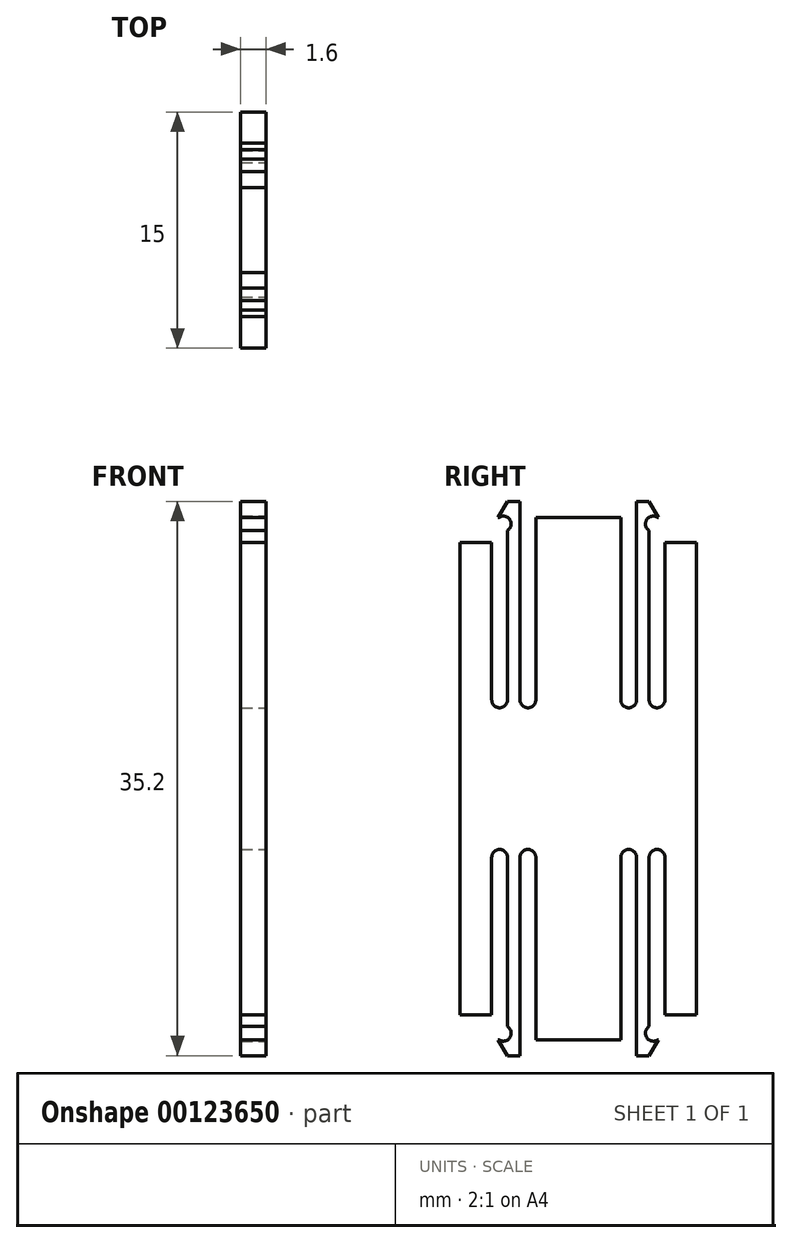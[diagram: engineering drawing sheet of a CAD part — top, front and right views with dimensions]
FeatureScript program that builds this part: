
annotation { "Feature Type Name" : "Feature", "Feature Type Description" : "" }
export const myFeature = defineFeature(function(context is Context, id is Id, definition is map)
    precondition{}
    {
        {
            var Q0;
            Q0=qCreatedBy(makeId("Right.planeOp"),FACE);
            var sketch = newSketch(context, id + "F3", { "sketchPlane" : qUnion([Q0])});
            skLineSegment(sketch, "E0.bottom", {"start": v(0, 0) * mm, "end": v(15, 0) * mm});
            skLineSegment(sketch, "E0.top", {"start": v(0, 30) * mm, "end": v(15, 30) * mm});
            skLineSegment(sketch, "E0.left", {"start": v(0, 0) * mm, "end": v(0, 30) * mm});
            skLineSegment(sketch, "E0.right", {"start": v(15, 0) * mm, "end": v(15, 30) * mm});
            skSolve(sketch);
        }
        {
            var Q0;
            Q0=makeQuery(id+"F3.imprint","IMPRINT",FACE,{"disambiguationData":[TD([[makeQuery(id+"F3.imprint","IMPRINT",EDGE,{"derivedFrom":sQuery(id+"F3.wireOp",EDGE,"E0.bottom")}),1.0]])]});
            extrude(context, id + "F4", {"entities" : qUnion([Q0]), "depth" : 1.6 * mm});
        }
        {
            var Q0;
            Q0=makeQuery(id+"F4.opExtrude","CAP_FACE",FACE,{"disambiguationData":[OSD([sQuery(id+"F3.wireOp",EDGE,"E0.bottom"),sQuery(id+"F3.wireOp",EDGE,"E0.top"),sQuery(id+"F3.wireOp",EDGE,"E0.left"),sQuery(id+"F3.wireOp",EDGE,"E0.right")])],"isStart":false});
            var sketch = newSketch(context, id + "F5", { "sketchPlane" : qUnion([Q0])});
            skLineSegment(sketch, "E1", {"start": v(2, 30) * mm, "end": v(2, 20) * mm});
            skLineSegment(sketch, "E2", {"start": v(2, 20) * mm, "end": v(3, 20) * mm});
            skLineSegment(sketch, "E3", {"start": v(3, 20) * mm, "end": v(3, 30) * mm});
            skLineSegment(sketch, "E4", {"start": v(3.8, 30) * mm, "end": v(3.8, 20) * mm});
            skLineSegment(sketch, "E5", {"start": v(3.8, 20) * mm, "end": v(4.8, 20) * mm});
            skLineSegment(sketch, "E6", {"start": v(4.8, 20) * mm, "end": v(4.8, 30) * mm});
            skLineSegment(sketch, "E7", {"start": v(2, 30) * mm, "end": v(3, 30) * mm});
            skLineSegment(sketch, "E8", {"start": v(3.8, 30) * mm, "end": v(4.8, 30) * mm});
            skLineSegment(sketch, "E9", {"start": v(7.5, 30) * mm, "end": v(7.5, 0) * mm, "construction": true});
            skLineSegment(sketch, "E10", {"start": v(0, 15) * mm, "end": v(15, 15) * mm, "construction": true});
            skLineSegment(sketch, "E11.MirrorCS", {"start": v(10.2, 20) * mm, "end": v(10.2, 30) * mm});
            skLineSegment(sketch, "E12.MirrorCS", {"start": v(12, 20) * mm, "end": v(12, 30) * mm});
            skLineSegment(sketch, "E13.MirrorCS", {"start": v(13, 30) * mm, "end": v(13, 20) * mm});
            skLineSegment(sketch, "E14.MirrorCS", {"start": v(11.2, 30) * mm, "end": v(11.2, 20) * mm});
            skLineSegment(sketch, "E15.MirrorCS", {"start": v(11.2, 20) * mm, "end": v(10.2, 20) * mm});
            skLineSegment(sketch, "E16.MirrorCS", {"start": v(13, 20) * mm, "end": v(12, 20) * mm});
            skLineSegment(sketch, "E17.MirrorCS", {"start": v(11.2, 30) * mm, "end": v(10.2, 30) * mm});
            skLineSegment(sketch, "E18.MirrorCS", {"start": v(13, 30) * mm, "end": v(12, 30) * mm});
            skLineSegment(sketch, "E19.MirrorCS", {"start": v(12, 10) * mm, "end": v(12, 0) * mm});
            skLineSegment(sketch, "E20.MirrorCS", {"start": v(13, 0) * mm, "end": v(13, 10) * mm});
            skLineSegment(sketch, "E21.MirrorCS", {"start": v(13, 10) * mm, "end": v(12, 10) * mm});
            skLineSegment(sketch, "E22.MirrorCS", {"start": v(11.2, 10) * mm, "end": v(10.2, 10) * mm});
            skLineSegment(sketch, "E23.MirrorCS", {"start": v(11.2, 0) * mm, "end": v(10.2, 0) * mm});
            skLineSegment(sketch, "E24.MirrorCS", {"start": v(13, 0) * mm, "end": v(12, 0) * mm});
            skLineSegment(sketch, "E25.MirrorCS", {"start": v(10.2, 10) * mm, "end": v(10.2, 0) * mm});
            skLineSegment(sketch, "E26.MirrorCS", {"start": v(11.2, 0) * mm, "end": v(11.2, 10) * mm});
            skLineSegment(sketch, "E27.MirrorCS", {"start": v(4.8, 10) * mm, "end": v(4.8, 0) * mm});
            skLineSegment(sketch, "E28.MirrorCS", {"start": v(3.8, 0) * mm, "end": v(3.8, 10) * mm});
            skLineSegment(sketch, "E29.MirrorCS", {"start": v(3, 10) * mm, "end": v(3, 0) * mm});
            skLineSegment(sketch, "E30.MirrorCS", {"start": v(2, 10) * mm, "end": v(3, 10) * mm});
            skLineSegment(sketch, "E31.MirrorCS", {"start": v(3.8, 10) * mm, "end": v(4.8, 10) * mm});
            skLineSegment(sketch, "E32.MirrorCS", {"start": v(2, 0) * mm, "end": v(3, 0) * mm});
            skLineSegment(sketch, "E33.MirrorCS", {"start": v(3.8, 0) * mm, "end": v(4.8, 0) * mm});
            skLineSegment(sketch, "E34.MirrorCS", {"start": v(2, 0) * mm, "end": v(2, 10) * mm});
            skSolve(sketch);
        }
        {
            var Q0;
            Q0 = qSketchRegion(id + "F5", true);
            extrude(context, id + "F0", {"entities" : qUnion([Q0]), "operationType" : NewBodyOperationType.REMOVE, "oppositeDirection" : true, "depth" : 25 * mm});
        }
        {
            var Q0;
            Q0=makeQuery(id+"F4.opExtrude","CAP_FACE",FACE,{"disambiguationData":[OSD([sQuery(id+"F3.wireOp",EDGE,"E0.bottom"),sQuery(id+"F3.wireOp",EDGE,"E0.top"),sQuery(id+"F3.wireOp",EDGE,"E0.left"),sQuery(id+"F3.wireOp",EDGE,"E0.right")])],"isStart":false});
            var sketch = newSketch(context, id + "F6", { "sketchPlane" : qUnion([Q0])});
            skLineSegment(sketch, "E35", {"start": v(3.8, 30) * mm, "end": v(3.8, 32.6) * mm});
            skLineSegment(sketch, "E36", {"start": v(3.8, 32.6) * mm, "end": v(3, 32.6) * mm});
            skLineSegment(sketch, "E37", {"start": v(3, 32.6) * mm, "end": v(2.4, 31.6) * mm});
            skLineSegment(sketch, "E38", {"start": v(2.4, 31.6) * mm, "end": v(3, 31.6) * mm});
            skLineSegment(sketch, "E39", {"start": v(3, 31.6) * mm, "end": v(3, 30) * mm});
            skLineSegment(sketch, "E40", {"start": v(3, 30) * mm, "end": v(3, 30) * mm});
            skLineSegment(sketch, "E41.bottom", {"start": v(4.8, 30) * mm, "end": v(7.5, 30) * mm});
            skLineSegment(sketch, "E41.top", {"start": v(4.8, 31.6) * mm, "end": v(7.5, 31.6) * mm});
            skLineSegment(sketch, "E41.left", {"start": v(4.8, 30) * mm, "end": v(4.8, 31.6) * mm});
            skLineSegment(sketch, "E41.right", {"start": v(7.5, 30) * mm, "end": v(7.5, 31.6) * mm});
            skLineSegment(sketch, "E42", {"start": v(0, 15) * mm, "end": v(15, 15) * mm, "construction": true});
            skLineSegment(sketch, "E43", {"start": v(7.5, 15) * mm, "end": v(7.5, 30) * mm, "construction": true});
            skLineSegment(sketch, "E44", {"start": v(3, 30) * mm, "end": v(3.8, 30) * mm});
            skLineSegment(sketch, "E45.MirrorCS", {"start": v(10.2, 30) * mm, "end": v(7.5, 30) * mm});
            skLineSegment(sketch, "E46.MirrorCS", {"start": v(10.2, 31.6) * mm, "end": v(7.5, 31.6) * mm});
            skLineSegment(sketch, "E47.MirrorCS", {"start": v(10.2, 30) * mm, "end": v(10.2, 31.6) * mm});
            skLineSegment(sketch, "E48.MirrorCS", {"start": v(11.2, 32.6) * mm, "end": v(12, 32.6) * mm});
            skLineSegment(sketch, "E49.MirrorCS", {"start": v(12, 32.6) * mm, "end": v(12.6, 31.6) * mm});
            skLineSegment(sketch, "E50.MirrorCS", {"start": v(12.6, 31.6) * mm, "end": v(12, 31.6) * mm});
            skLineSegment(sketch, "E51.MirrorCS", {"start": v(12, 30) * mm, "end": v(11.2, 30) * mm});
            skLineSegment(sketch, "E52.MirrorCS", {"start": v(11.2, 30) * mm, "end": v(11.2, 32.6) * mm});
            skLineSegment(sketch, "E53.MirrorCS", {"start": v(12, 31.6) * mm, "end": v(12, 30) * mm});
            skLineSegment(sketch, "E54.MirrorCS", {"start": v(3, -2.6) * mm, "end": v(2.4, -1.6) * mm});
            skLineSegment(sketch, "E55.MirrorCS", {"start": v(4.8, -1.6) * mm, "end": v(7.5, -1.6) * mm});
            skLineSegment(sketch, "E56.MirrorCS", {"start": v(4.8, 0) * mm, "end": v(4.8, -1.6) * mm});
            skLineSegment(sketch, "E57.MirrorCS", {"start": v(10.2, 0) * mm, "end": v(7.5, 0) * mm});
            skLineSegment(sketch, "E58.MirrorCS", {"start": v(10.2, -1.6) * mm, "end": v(7.5, -1.6) * mm});
            skLineSegment(sketch, "E59.MirrorCS", {"start": v(10.2, 0) * mm, "end": v(10.2, -1.6) * mm});
            skLineSegment(sketch, "E60.MirrorCS", {"start": v(11.2, 0) * mm, "end": v(11.2, -2.6) * mm});
            skLineSegment(sketch, "E61.MirrorCS", {"start": v(12, -1.6) * mm, "end": v(12, 0) * mm});
            skLineSegment(sketch, "E62.MirrorCS", {"start": v(4.8, 0) * mm, "end": v(7.5, 0) * mm});
            skLineSegment(sketch, "E63.MirrorCS", {"start": v(3, -1.6) * mm, "end": v(3, 0) * mm});
            skLineSegment(sketch, "E64.MirrorCS", {"start": v(3.8, 0) * mm, "end": v(3.8, -2.6) * mm});
            skLineSegment(sketch, "E65.MirrorCS", {"start": v(3.8, -2.6) * mm, "end": v(3, -2.6) * mm});
            skLineSegment(sketch, "E66.MirrorCS", {"start": v(2.4, -1.6) * mm, "end": v(3, -1.6) * mm});
            skLineSegment(sketch, "E67.MirrorCS", {"start": v(12, -2.6) * mm, "end": v(12.6, -1.6) * mm});
            skLineSegment(sketch, "E68.MirrorCS", {"start": v(12.6, -1.6) * mm, "end": v(12, -1.6) * mm});
            skLineSegment(sketch, "E69.MirrorCS", {"start": v(11.2, -2.6) * mm, "end": v(12, -2.6) * mm});
            skLineSegment(sketch, "E70.MirrorCS", {"start": v(3, 0) * mm, "end": v(3.8, 0) * mm});
            skLineSegment(sketch, "E71.MirrorCS", {"start": v(12, 0) * mm, "end": v(11.2, 0) * mm});
            skSolve(sketch);
        }
        {
            var Q0;
            Q0 = qSketchRegion(id + "F6", true);
            extrude(context, id + "F1", {"entities" : qUnion([Q0]), "operationType" : NewBodyOperationType.ADD, "oppositeDirection" : true, "depth" : 1.6 * mm});
        }
        {
            var Q0;
            Q0=makeQuery(id+"F1.boolean.opBoolean","MERGE",FACE,{"derivedFrom":[makeQuery(id+"F4.opExtrude","CAP_FACE",FACE,{"disambiguationData":[OSD([sQuery(id+"F3.wireOp",EDGE,"E0.bottom"),sQuery(id+"F3.wireOp",EDGE,"E0.top"),sQuery(id+"F3.wireOp",EDGE,"E0.left"),sQuery(id+"F3.wireOp",EDGE,"E0.right")])],"isStart":false}),makeQuery(id+"F1.opExtrude","CAP_FACE",FACE,{"disambiguationData":[OSD([sQuery(id+"F6.wireOp",EDGE,"E35"),sQuery(id+"F6.wireOp",EDGE,"E36"),sQuery(id+"F6.wireOp",EDGE,"E37"),sQuery(id+"F6.wireOp",EDGE,"E38"),sQuery(id+"F6.wireOp",EDGE,"E39"),sQuery(id+"F6.wireOp",EDGE,"E44")])],"isStart":true}),makeQuery(id+"F1.opExtrude","CAP_FACE",FACE,{"disambiguationData":[OSD([sQuery(id+"F6.wireOp",EDGE,"E41.bottom"),sQuery(id+"F6.wireOp",EDGE,"E41.top"),sQuery(id+"F6.wireOp",EDGE,"E41.left"),sQuery(id+"F6.wireOp",EDGE,"E45.MirrorCS"),sQuery(id+"F6.wireOp",EDGE,"E46.MirrorCS"),sQuery(id+"F6.wireOp",EDGE,"E47.MirrorCS")])],"isStart":true}),makeQuery(id+"F1.opExtrude","CAP_FACE",FACE,{"disambiguationData":[OSD([sQuery(id+"F6.wireOp",EDGE,"E48.MirrorCS"),sQuery(id+"F6.wireOp",EDGE,"E49.MirrorCS"),sQuery(id+"F6.wireOp",EDGE,"E50.MirrorCS"),sQuery(id+"F6.wireOp",EDGE,"E51.MirrorCS"),sQuery(id+"F6.wireOp",EDGE,"E52.MirrorCS"),sQuery(id+"F6.wireOp",EDGE,"E53.MirrorCS")])],"isStart":true}),makeQuery(id+"F1.opExtrude","CAP_FACE",FACE,{"disambiguationData":[OSD([sQuery(id+"F6.wireOp",EDGE,"E54.MirrorCS"),sQuery(id+"F6.wireOp",EDGE,"E63.MirrorCS"),sQuery(id+"F6.wireOp",EDGE,"E64.MirrorCS"),sQuery(id+"F6.wireOp",EDGE,"E65.MirrorCS"),sQuery(id+"F6.wireOp",EDGE,"E66.MirrorCS"),sQuery(id+"F6.wireOp",EDGE,"E70.MirrorCS")])],"isStart":true}),makeQuery(id+"F1.opExtrude","CAP_FACE",FACE,{"disambiguationData":[OSD([sQuery(id+"F6.wireOp",EDGE,"E55.MirrorCS"),sQuery(id+"F6.wireOp",EDGE,"E56.MirrorCS"),sQuery(id+"F6.wireOp",EDGE,"E57.MirrorCS"),sQuery(id+"F6.wireOp",EDGE,"E58.MirrorCS"),sQuery(id+"F6.wireOp",EDGE,"E59.MirrorCS"),sQuery(id+"F6.wireOp",EDGE,"E62.MirrorCS")])],"isStart":true}),makeQuery(id+"F1.opExtrude","CAP_FACE",FACE,{"disambiguationData":[OSD([sQuery(id+"F6.wireOp",EDGE,"E60.MirrorCS"),sQuery(id+"F6.wireOp",EDGE,"E61.MirrorCS"),sQuery(id+"F6.wireOp",EDGE,"E67.MirrorCS"),sQuery(id+"F6.wireOp",EDGE,"E68.MirrorCS"),sQuery(id+"F6.wireOp",EDGE,"E69.MirrorCS"),sQuery(id+"F6.wireOp",EDGE,"E71.MirrorCS")])],"isStart":true})]});
            var sketch = newSketch(context, id + "F2", { "sketchPlane" : qUnion([Q0])});
            skCircle(sketch, "E72", {"center": v(4.3, 20) * mm, "radius": 0.5 * mm});
            skCircle(sketch, "E73", {"center": v(2.74, 31.18) * mm, "radius": 0.5 * mm});
            skPoint(sketch, "E74", {"position": v(3, 31.6) * mm});
            skLineSegment(sketch, "E75", {"start": v(3, 31.6) * mm, "end": v(2, 30) * mm, "construction": true});
            skLineSegment(sketch, "E76", {"start": v(2, 30) * mm, "end": v(2, 30) * mm});
            skCircle(sketch, "E77", {"center": v(2.5, 20) * mm, "radius": 0.5 * mm});
            skLineSegment(sketch, "E78", {"start": v(7.5, 31.6) * mm, "end": v(7.5, -1.6) * mm, "construction": true});
            skLineSegment(sketch, "E79", {"start": v(0, 15) * mm, "end": v(15, 15) * mm, "construction": true});
            skCircle(sketch, "E80.MirrorC", {"center": v(10.7, 20) * mm, "radius": 0.5 * mm});
            skCircle(sketch, "E81.MirrorC", {"center": v(12.5, 20) * mm, "radius": 0.5 * mm});
            skCircle(sketch, "E82.MirrorC", {"center": v(12.26, 31.18) * mm, "radius": 0.5 * mm});
            skCircle(sketch, "E83.MirrorC", {"center": v(12.26, -1.18) * mm, "radius": 0.5 * mm});
            skCircle(sketch, "E84.MirrorC", {"center": v(12.5, 10) * mm, "radius": 0.5 * mm});
            skCircle(sketch, "E85.MirrorC", {"center": v(10.7, 10) * mm, "radius": 0.5 * mm});
            skCircle(sketch, "E86.MirrorC", {"center": v(4.3, 10) * mm, "radius": 0.5 * mm});
            skCircle(sketch, "E87.MirrorC", {"center": v(2.5, 10) * mm, "radius": 0.5 * mm});
            skCircle(sketch, "E88.MirrorC", {"center": v(2.74, -1.18) * mm, "radius": 0.5 * mm});
            skLineSegment(sketch, "E89", {"start": v(4.8, 31.6) * mm, "end": v(10.2, 31.6) * mm});
            skLineSegment(sketch, "E90", {"start": v(8.82, 31.6) * mm, "end": v(8.82, 31.6) * mm});
            skSolve(sketch);
        }
        {
            var Q0;
            Q0 = qSketchRegion(id + "F2", true);
            extrude(context, id + "F7", {"entities" : qUnion([Q0]), "operationType" : NewBodyOperationType.REMOVE, "oppositeDirection" : true, "depth" : 25 * mm});
        }
    });
